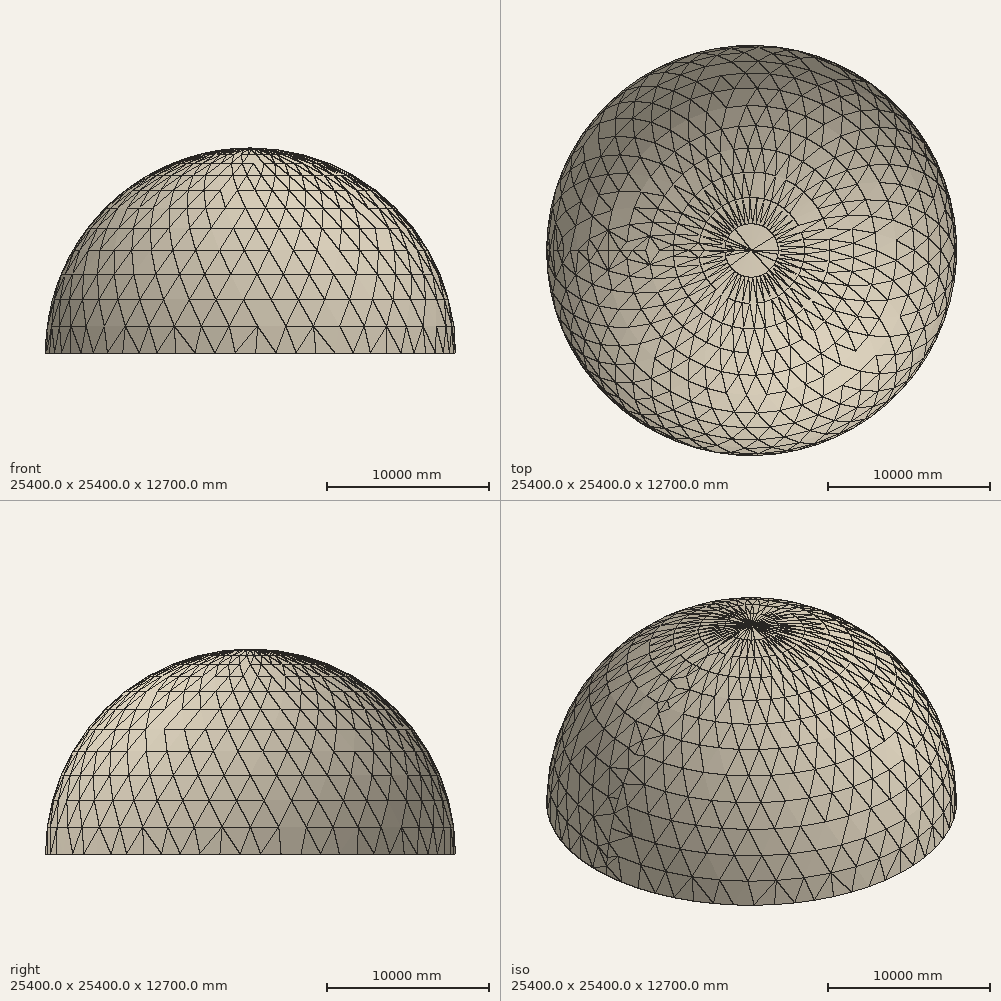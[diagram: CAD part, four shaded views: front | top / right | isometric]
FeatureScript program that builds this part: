
annotation { "Feature Type Name" : "Feature", "Feature Type Description" : "" }
export const myFeature = defineFeature(function(context is Context, id is Id, definition is map)
    precondition{}
    {
        {
            var Q0;
            Q0=qCreatedBy(makeId("Front.planeOp"),FACE);
            var sketch = newSketch(context, id + "F0", { "sketchPlane" : qUnion([Q0])});
            skArc(sketch, "E0", {"start": v(-12700, 0) * mm, "mid": v(-8980.26, 8980.26) * mm, "end": v(0, 12700) * mm});
            skArc(sketch, "E1", {"start": v(-12573, 0) * mm, "mid": v(-8890.45, 8890.45) * mm, "end": v(0, 12573) * mm});
            skLineSegment(sketch, "E2", {"start": v(-12700, 0) * mm, "end": v(-12573, 0) * mm});
            skLineSegment(sketch, "E3", {"start": v(0, 12700) * mm, "end": v(0, 12573) * mm});
            skLineSegment(sketch, "E4", {"start": v(0, 0) * mm, "end": v(0, 16895.03) * mm, "construction": true});
            skSolve(sketch);
        }
        {
            var Q0;
            Q0 = qSketchRegion(id + "F0", true);
            var Q1;
            Q1=sQuery(id+"F0.wireOp",EDGE,"E4");
            revolve(context, id + "F1", {"entities" : qUnion([Q0]), "axis" : qUnion([Q1]), "revolveType" : RevolveType.FULL});
        }
    });
